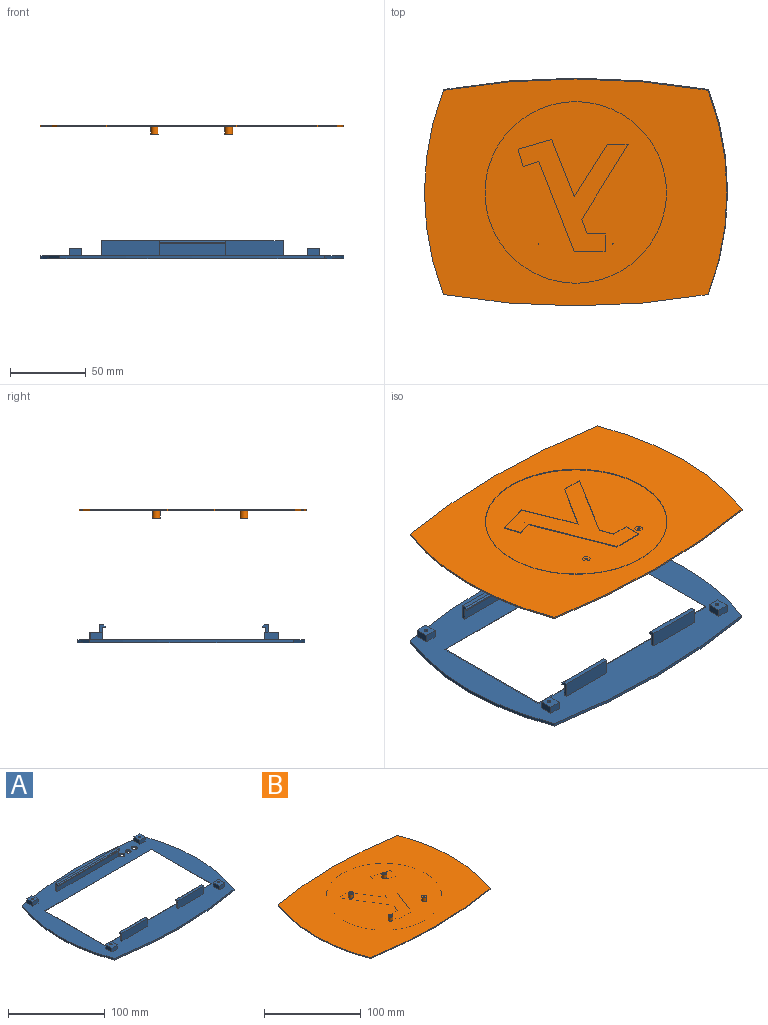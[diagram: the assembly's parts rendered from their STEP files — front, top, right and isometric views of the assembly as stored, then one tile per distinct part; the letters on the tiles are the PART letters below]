
ASSEMBLY  parts=2 mates=2
PART A: 71 faces, bbox 200x150x12 mm
  f0: plane 8.42x5mm, normal (-1,0,0), area 42.1mm2, adj f2,f6,f12,f70
  f1: plane 5x4.03mm, normal (0,1,0), area 20.2mm2, adj f2,f6,f13,f70
  f2: plane 9x8mm, normal (0,0,1), area 65.9mm2, adj f0,f1,f12,f13,f40,f70
  f3: plane 7.98x5mm, normal (1,0,0), area 39.9mm2, adj f5,f6,f15,f69
  f4: plane 5x1.18mm, normal (0,1,0), area 5.9mm2, adj f5,f6,f14,f69
  f5: plane 9x8mm, normal (0,0,1), area 63.7mm2, adj f3,f4,f14,f15,f38,f69
  f6: plane 200x150mm, normal (0,0,1), area 13370.6mm2, adj f0,f1,f3,f4,f7,f8,f9,f10
  f7: cylinder r=188.5mm len=135mm, axis (0,0,1), area 276.1mm2, adj f6,f8,f10,f11
  f8: cylinder r=514.17mm len=175mm, axis (0,0,1), area 351.7mm2, adj f6,f7,f9,f11
  f9: cylinder r=188.5mm len=135mm, axis (0,0,1), area 276.1mm2, adj f6,f8,f10,f11
  f10: cylinder r=514.17mm len=175mm, axis (0,0,1), area 351.7mm2, adj f6,f7,f9,f11
  f11: plane 200x150mm, normal (0,0,-1), area 11941.3mm2, adj f7,f8,f9,f10,f30,f31,f32,f33
  f12: plane 8x5mm, normal (0,-1,0), area 40mm2, adj f0,f2,f6,f13
  f13: plane 9x5mm, normal (1,0,0), area 45mm2, adj f1,f2,f6,f12
  f14: plane 9x5mm, normal (-1,0,0), area 45mm2, adj f4,f5,f6,f15
  f15: plane 8x5mm, normal (0,-1,0), area 40mm2, adj f3,f5,f6,f14
  f16: plane 9x5mm, normal (-1,0,0), area 45mm2, adj f6,f17,f19,f20
  f17: plane 8x5mm, normal (0,-1,0), area 40mm2, adj f6,f16,f18,f20
  f18: plane 9x5mm, normal (1,0,0), area 45mm2, adj f6,f17,f19,f20
  f19: plane 8x5mm, normal (0,1,0), area 40mm2, adj f6,f16,f18,f20
  f20: plane 9x8mm, normal (0,0,1), area 67.1mm2, adj f16,f17,f18,f19,f36
  f21: plane 9x5mm, normal (-1,0,0), area 45mm2, adj f6,f22,f24,f25
  f22: plane 8x5mm, normal (0,-1,0), area 40mm2, adj f6,f21,f23,f25
  f23: plane 9x5mm, normal (1,0,0), area 45mm2, adj f6,f22,f24,f25
  f24: plane 8x5mm, normal (0,1,0), area 40mm2, adj f6,f21,f23,f25
  f25: plane 9x8mm, normal (0,0,1), area 67.1mm2, adj f21,f22,f23,f24,f34
  f26: plane 157.07x0.54mm, normal (0,0.71,-0.71), area 118.6mm2, adj f6,f27,f28,f30
  f27: plane 88.07x0.54mm, normal (0.71,0,-0.71), area 66.3mm2, adj f6,f26,f29,f32
  f28: plane 88.07x0.54mm, normal (-0.71,0,-0.71), area 66.3mm2, adj f6,f26,f29,f31
  f29: plane 157.07x0.54mm, normal (0,-0.71,-0.71), area 118.6mm2, adj f6,f27,f28,f33
  f30: cylinder r=5mm len=164.14mm, axis (-1,0,0), area 629.9mm2, adj f11,f26,f31,f32
  f31: cylinder r=5mm len=95.14mm, axis (0,-1,0), area 359mm2, adj f11,f28,f30,f33
  f32: cylinder r=5mm len=95.14mm, axis (0,-1,0), area 359mm2, adj f11,f27,f30,f33
  f33: cylinder r=5mm len=164.14mm, axis (-1,0,0), area 629.9mm2, adj f11,f29,f31,f32
  f34: cylinder r=1.25mm len=5mm, axis (0,0,1), area 39.3mm2, adj f25,f35
  f35: cone r=0mm half-angle=59deg, axis (0,0,1), area 5.7mm2, adj f34
  f36: cylinder r=1.25mm len=5mm, axis (0,0,1), area 39.3mm2, adj f20,f37
  f37: cone r=0mm half-angle=59deg, axis (0,0,1), area 5.7mm2, adj f36
  f38: cylinder r=1.25mm len=5mm, axis (0,0,1), area 39.3mm2, adj f5,f39
  f39: cone r=0mm half-angle=59deg, axis (0,0,1), area 5.7mm2, adj f38
  f40: cylinder r=1.25mm len=5mm, axis (0,0,1), area 39.3mm2, adj f2,f41
  f41: cone r=0mm half-angle=59deg, axis (0,0,1), area 5.7mm2, adj f40
  f42: cylinder r=3mm len=6mm, axis (0,0,-1), area 37.7mm2, adj f6,f11
  f43: cylinder r=3mm len=6mm, axis (0,0,-1), area 37.7mm2, adj f6,f11
  f44: cylinder r=3mm len=6mm, axis (0,0,-1), area 37.7mm2, adj f6,f11
  f45: plane 10x4mm, normal (-1,0,0), area 23.5mm2, adj f6,f46,f48,f57,f58,f59,f68
  f46: plane 90x8mm, normal (0,-1,0), area 720mm2, adj f6,f45,f47,f57
  f47: plane 10x4mm, normal (1,0,0), area 23.5mm2, adj f6,f46,f48,f57,f58,f59,f68
  f48: plane 90x10mm, normal (0,1,0), area 900mm2, adj f6,f45,f47,f59
  f49: plane 38.01x8mm, normal (0,1,0), area 304.1mm2, adj f6,f50,f52,f65
  f50: plane 10x4mm, normal (-1,0,0), area 23.5mm2, adj f6,f49,f51,f63,f64,f65,f67
  f51: plane 38.01x10mm, normal (0,-1,0), area 380.1mm2, adj f6,f50,f52,f64
  f52: plane 10x4mm, normal (1,0,0), area 23.5mm2, adj f6,f49,f51,f63,f64,f65,f67
  f53: plane 38.01x10mm, normal (0,-1,0), area 380.1mm2, adj f6,f54,f56,f61
  f54: plane 10x4mm, normal (1,0,0), area 23.5mm2, adj f6,f53,f55,f60,f61,f62,f66
  f55: plane 38.01x8mm, normal (0,1,0), area 304.1mm2, adj f6,f54,f56,f62
  f56: plane 10x4mm, normal (-1,0,0), area 23.5mm2, adj f6,f53,f55,f60,f61,f62,f66
  f57: plane 90x2mm, normal (0,0,-1), area 180mm2, adj f45,f46,f47,f58
  f58: plane 90x1mm, normal (0,-1,0), area 90mm2, adj f45,f47,f57,f68
  f59: plane 90x3mm, normal (0,0,1), area 270mm2, adj f45,f47,f48,f68
  f60: plane 38.01x1mm, normal (0,1,0), area 38mm2, adj f54,f56,f62,f66
  f61: plane 38.01x3mm, normal (0,0,1), area 114mm2, adj f53,f54,f56,f66
  f62: plane 38.01x2mm, normal (0,0,-1), area 76mm2, adj f54,f55,f56,f60
  f63: plane 38.01x1mm, normal (0,1,0), area 38mm2, adj f50,f52,f65,f67
  f64: plane 38.01x3mm, normal (0,0,1), area 114mm2, adj f50,f51,f52,f67
  f65: plane 38.01x2mm, normal (0,0,-1), area 76mm2, adj f49,f50,f52,f63
  f66: plane 38.01x1mm, normal (0,0.71,0.71), area 53.8mm2, adj f54,f56,f60,f61
  f67: plane 38.01x1mm, normal (0,0.71,0.71), area 53.8mm2, adj f50,f52,f63,f64
  f68: plane 90x1mm, normal (0,-0.71,0.71), area 127.3mm2, adj f45,f47,f58,f59
  f69: cylinder r=543.21mm len=6.82mm, axis (0,0,-1), area 34.5mm2, adj f3,f4,f5,f6
  f70: cylinder r=543.21mm len=5mm, axis (0,0,-1), area 20.1mm2, adj f0,f1,f2,f6
PART B: 104 faces, bbox 200x150x6 mm
  f0: plane 200x150mm, normal (0,0,-1), area 16368.8mm2, adj f1,f2,f3,f4,f17,f18,f19,f20
  f1: cylinder r=188.5mm len=135mm, axis (0,0,-1), area 138.1mm2, adj f0,f2,f4,f5
  f2: cylinder r=514.17mm len=175mm, axis (0,0,-1), area 175.9mm2, adj f0,f1,f3,f5
  f3: cylinder r=188.5mm len=135mm, axis (0,0,-1), area 138.1mm2, adj f0,f2,f4,f5
  f4: cylinder r=514.17mm len=175mm, axis (0,0,-1), area 175.9mm2, adj f0,f1,f3,f5
  f5: plane 200x150mm, normal (0,0,1), area 27564.4mm2, adj f1,f2,f3,f4,f88,f90,f92,f94
  f6: plane 11.53x3.43mm, normal (0.96,-0.29,0), area 6mm2, adj f7,f85,f86,f87
  f7: plane 22.2x6.41mm, normal (0.28,0.96,0), area 11.6mm2, adj f6,f8,f86,f87
  f8: plane 37.86x14.94mm, normal (-0.93,0.37,0), area 20.3mm2, adj f7,f9,f86,f87
  f9: plane 34.5x21.9mm, normal (0.84,0.54,0), area 20.4mm2, adj f8,f10,f86,f87
  f10: plane 13.73x0.5mm, normal (0,1,0), area 6.9mm2, adj f9,f11,f86,f87
  f11: plane 49.39x30.58mm, normal (-0.85,-0.53,0), area 29mm2, adj f10,f12,f86,f87
  f12: plane 9.76x3.43mm, normal (-0.94,0.33,0), area 5.2mm2, adj f11,f13,f86,f87
  f13: plane 11.91x0.5mm, normal (0,1,0), area 6mm2, adj f12,f14,f86,f87
  f14: plane 11.63x0.5mm, normal (-1,0,0), area 5.8mm2, adj f13,f15,f86,f87
  f15: plane 20.39x0.5mm, normal (0,-1,0), area 10.2mm2, adj f14,f16,f86,f87
  f16: plane 59.54x23.41mm, normal (0.93,-0.37,0), area 32mm2, adj f15,f85,f86,f87
  f17: plane 3.06x0.5mm, normal (-1,0,0), area 1.5mm2, adj f0,f18,f84,f86
  f18: plane 4.6x0.5mm, normal (-1,0.07,0), area 2.3mm2, adj f0,f17,f19,f86
  f19: plane 5.95x0.91mm, normal (-0.99,0.15,0), area 3mm2, adj f0,f18,f20,f86
  f20: plane 5.74x1.48mm, normal (-0.97,0.25,0), area 3mm2, adj f0,f19,f21,f86
  f21: plane 5.51x2.02mm, normal (-0.94,0.34,0), area 2.9mm2, adj f0,f20,f22,f86
  f22: plane 5.24x2.52mm, normal (-0.9,0.43,0), area 2.9mm2, adj f0,f21,f23,f86
  f23: plane 4.94x3mm, normal (-0.85,0.52,0), area 2.9mm2, adj f0,f22,f24,f86
  f24: plane 4.61x3.45mm, normal (-0.8,0.6,0), area 2.9mm2, adj f0,f23,f25,f86
  f25: plane 4.26x3.87mm, normal (-0.74,0.67,0), area 2.9mm2, adj f0,f24,f26,f86
  f26: plane 4.26x3.87mm, normal (-0.67,0.74,0), area 2.9mm2, adj f0,f25,f27,f86
  f27: plane 4.61x3.45mm, normal (-0.6,0.8,0), area 2.9mm2, adj f0,f26,f28,f86
  f28: plane 4.94x3mm, normal (-0.52,0.85,0), area 2.9mm2, adj f0,f27,f29,f86
  f29: plane 5.24x2.52mm, normal (-0.43,0.9,0), area 2.9mm2, adj f0,f28,f30,f86
  f30: plane 5.51x2.02mm, normal (-0.34,0.94,0), area 2.9mm2, adj f0,f29,f31,f86
  f31: plane 5.74x1.48mm, normal (-0.25,0.97,0), area 3mm2, adj f0,f30,f32,f86
  f32: plane 5.95x0.91mm, normal (-0.15,0.99,0), area 3mm2, adj f0,f31,f33,f86
  f33: plane 4.6x0.5mm, normal (-0.07,1,0), area 2.3mm2, adj f0,f32,f34,f86
  f34: plane 3.06x0.5mm, normal (0,1,0), area 1.5mm2, adj f0,f33,f35,f86
  f35: plane 4.6x0.5mm, normal (0.07,1,0), area 2.3mm2, adj f0,f34,f36,f86
  f36: plane 5.95x0.91mm, normal (0.15,0.99,0), area 3mm2, adj f0,f35,f37,f86
  f37: plane 5.75x1.48mm, normal (0.25,0.97,0), area 3mm2, adj f0,f36,f38,f86
  f38: plane 5.51x2.02mm, normal (0.34,0.94,0), area 2.9mm2, adj f0,f37,f39,f86
  f39: plane 5.24x2.52mm, normal (0.43,0.9,0), area 2.9mm2, adj f0,f38,f40,f86
  f40: plane 4.94x3mm, normal (0.52,0.85,0), area 2.9mm2, adj f0,f39,f41,f86
  f41: plane 4.61x3.45mm, normal (0.6,0.8,0), area 2.9mm2, adj f0,f40,f42,f86
  f42: plane 4.26x3.87mm, normal (0.67,0.74,0), area 2.9mm2, adj f0,f41,f43,f86
  f43: plane 4.26x3.87mm, normal (0.74,0.67,0), area 2.9mm2, adj f0,f42,f44,f86
  f44: plane 4.61x3.45mm, normal (0.8,0.6,0), area 2.9mm2, adj f0,f43,f45,f86
  f45: plane 4.94x3mm, normal (0.85,0.52,0), area 2.9mm2, adj f0,f44,f46,f86
  f46: plane 5.24x2.52mm, normal (0.9,0.43,0), area 2.9mm2, adj f0,f45,f47,f86
  f47: plane 5.51x2.02mm, normal (0.94,0.34,0), area 2.9mm2, adj f0,f46,f48,f86
  f48: plane 5.74x1.48mm, normal (0.97,0.25,0), area 3mm2, adj f0,f47,f49,f86
  f49: plane 5.95x0.91mm, normal (0.99,0.15,0), area 3mm2, adj f0,f48,f50,f86
  f50: plane 4.6x0.5mm, normal (1,0.07,0), area 2.3mm2, adj f0,f49,f51,f86
  f51: plane 3.06x0.5mm, normal (1,0,0), area 1.5mm2, adj f0,f50,f52,f86
  f52: plane 4.6x0.5mm, normal (1,-0.07,0), area 2.3mm2, adj f0,f51,f53,f86
  f53: plane 5.95x0.91mm, normal (0.99,-0.15,0), area 3mm2, adj f0,f52,f54,f86
  f54: plane 5.75x1.48mm, normal (0.97,-0.25,0), area 3mm2, adj f0,f53,f55,f86
  f55: plane 5.51x2.02mm, normal (0.94,-0.34,0), area 2.9mm2, adj f0,f54,f56,f86
  f56: plane 5.24x2.52mm, normal (0.9,-0.43,0), area 2.9mm2, adj f0,f55,f57,f86
  f57: plane 4.94x3mm, normal (0.85,-0.52,0), area 2.9mm2, adj f0,f56,f58,f86
  f58: plane 4.61x3.45mm, normal (0.8,-0.6,0), area 2.9mm2, adj f0,f57,f59,f86
  f59: plane 4.26x3.87mm, normal (0.74,-0.67,0), area 2.9mm2, adj f0,f58,f60,f86
  f60: plane 4.26x3.87mm, normal (0.67,-0.74,0), area 2.9mm2, adj f0,f59,f61,f86
  f61: plane 4.61x3.45mm, normal (0.6,-0.8,0), area 2.9mm2, adj f0,f60,f62,f86
  f62: plane 4.94x3mm, normal (0.52,-0.85,0), area 2.9mm2, adj f0,f61,f63,f86
  f63: plane 5.24x2.52mm, normal (0.43,-0.9,0), area 2.9mm2, adj f0,f62,f64,f86
  f64: plane 5.51x2.02mm, normal (0.34,-0.94,0), area 2.9mm2, adj f0,f63,f65,f86
  f65: plane 5.74x1.48mm, normal (0.25,-0.97,0), area 3mm2, adj f0,f64,f66,f86
  f66: plane 5.95x0.91mm, normal (0.15,-0.99,0), area 3mm2, adj f0,f65,f67,f86
  f67: plane 4.6x0.5mm, normal (0.07,-1,0), area 2.3mm2, adj f0,f66,f68,f86
  f68: plane 3.06x0.5mm, normal (0,-1,0), area 1.5mm2, adj f0,f67,f69,f86
  f69: plane 4.6x0.5mm, normal (-0.07,-1,0), area 2.3mm2, adj f0,f68,f70,f86
  f70: plane 5.95x0.91mm, normal (-0.15,-0.99,0), area 3mm2, adj f0,f69,f71,f86
  f71: plane 5.74x1.48mm, normal (-0.25,-0.97,0), area 3mm2, adj f0,f70,f72,f86
  f72: plane 5.51x2.02mm, normal (-0.34,-0.94,0), area 2.9mm2, adj f0,f71,f73,f86
  f73: plane 5.24x2.52mm, normal (-0.43,-0.9,0), area 2.9mm2, adj f0,f72,f74,f86
  f74: plane 4.94x3mm, normal (-0.52,-0.85,0), area 2.9mm2, adj f0,f73,f75,f86
  f75: plane 4.61x3.45mm, normal (-0.6,-0.8,0), area 2.9mm2, adj f0,f74,f76,f86
  f76: plane 4.26x3.87mm, normal (-0.67,-0.74,0), area 2.9mm2, adj f0,f75,f77,f86
  f77: plane 4.26x3.87mm, normal (-0.74,-0.67,0), area 2.9mm2, adj f0,f76,f78,f86
  f78: plane 4.61x3.45mm, normal (-0.8,-0.6,0), area 2.9mm2, adj f0,f77,f79,f86
  f79: plane 4.94x3mm, normal (-0.85,-0.52,0), area 2.9mm2, adj f0,f78,f80,f86
  f80: plane 5.24x2.52mm, normal (-0.9,-0.43,0), area 2.9mm2, adj f0,f79,f81,f86
  f81: plane 5.51x2.02mm, normal (-0.94,-0.34,0), area 2.9mm2, adj f0,f80,f82,f86
  f82: plane 5.75x1.48mm, normal (-0.97,-0.25,0), area 3mm2, adj f0,f81,f83,f86
  f83: plane 5.95x0.91mm, normal (-0.99,-0.15,0), area 3mm2, adj f0,f82,f84,f86
  f84: plane 4.6x0.5mm, normal (-1,-0.07,0), area 2.3mm2, adj f0,f17,f83,f86
  f85: plane 10.29x3.36mm, normal (-0.31,-0.95,0), area 5.4mm2, adj f6,f16,f86,f87
  f86: plane 119.88x119.88mm, normal (0,0,-1), area 9450.5mm2, adj f6,f7,f8,f9,f10,f11,f12,f13
  f87: plane 74.13x72.77mm, normal (0,0,-1), area 1823.5mm2, adj f6,f7,f8,f9,f10,f11,f12,f13
  f88: cylinder r=2.5mm len=5mm, axis (0,0,-1), area 78.5mm2, adj f5,f89
  f89: plane 5x5mm, normal (0,0,1), area 16.5mm2, adj f88,f96
  f90: cylinder r=2.5mm len=5mm, axis (0,0,-1), area 78.5mm2, adj f5,f91
  f91: plane 5x5mm, normal (0,0,1), area 16.5mm2, adj f90,f98
  f92: cylinder r=2.5mm len=5mm, axis (0,0,-1), area 78.5mm2, adj f5,f93
  f93: plane 5x5mm, normal (0,0,1), area 16.5mm2, adj f92,f102
  f94: cylinder r=2.5mm len=5mm, axis (0,0,-1), area 78.5mm2, adj f5,f95
  f95: plane 5x5mm, normal (0,0,1), area 16.5mm2, adj f94,f100
  f96: cylinder r=1mm len=5mm, axis (0,0,1), area 31.4mm2, adj f89,f97
  f97: cone r=0mm half-angle=59deg, axis (0,0,1), area 3.7mm2, adj f96
  f98: cylinder r=1mm len=5mm, axis (0,0,1), area 31.4mm2, adj f91,f99
  f99: cone r=0mm half-angle=59deg, axis (0,0,1), area 3.7mm2, adj f98
  f100: cylinder r=1mm len=5mm, axis (0,0,1), area 31.4mm2, adj f95,f101
  f101: cone r=0mm half-angle=59deg, axis (0,0,1), area 3.6mm2, adj f86,f100
  f102: cylinder r=1mm len=5mm, axis (0,0,1), area 31.4mm2, adj f93,f103
  f103: cone r=0mm half-angle=59deg, axis (0,0,1), area 3.6mm2, adj f86,f102
PLACE A t=(-2.75,31.57,0)mm
PLACE B rot(axis=(0,1,0),180deg) t=(-3.14,-91.14,66.54)mm
MATE slider B.f5 <-> A.f6  axis (0,0,-1) through (-3.14,-91.12,65.54)mm
MATE parallel B.f5 <-> A.f6  axis (0,0,-1) through (-3.14,-91.12,65.54)mm
